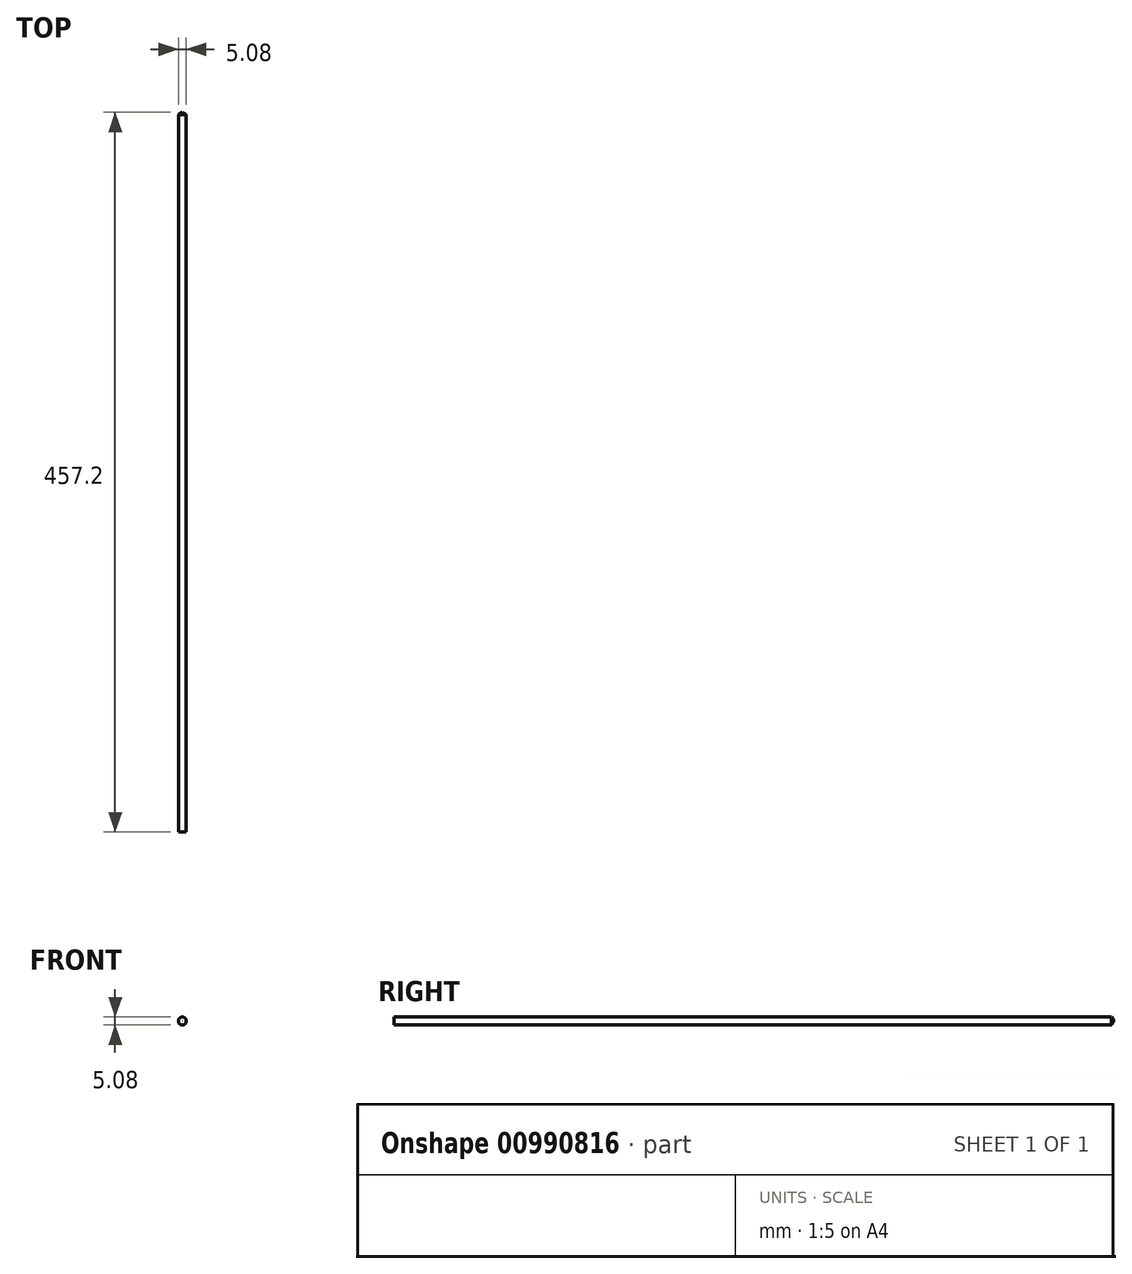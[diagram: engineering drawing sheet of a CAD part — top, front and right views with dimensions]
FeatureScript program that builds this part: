
annotation { "Feature Type Name" : "Feature", "Feature Type Description" : "" }
export const myFeature = defineFeature(function(context is Context, id is Id, definition is map)
    precondition{}
    {
        {
            var Q0;
            Q0=qCreatedBy(makeId("Front.planeOp"),FACE);
            var sketch = newSketch(context, id + "F0", { "sketchPlane" : qUnion([Q0])});
            skCircle(sketch, "E0", {"center": v(0, 0) * mm, "radius": 2.54 * mm});
            skSolve(sketch);
        }
        {
            var Q0;
            Q0 = qSketchRegion(id + "F0", true);
            extrude(context, id + "F1", {"entities" : qUnion([Q0]), "depth" : 457.2 * mm, "offsetDistance" : 25.4 * mm});
        }
        {
            var Q0;
            Q0=makeQuery(id+"F1.opExtrude","CAP_EDGE",EDGE,{"disambiguationData":[OSD([sQuery(id+"F0.wireOp",EDGE,"E0")])],"isStart":true});
            chamfer(context, id + "F2", {"entities" : qUnion([Q0]), "chamferType" : ChamferType.OFFSET_ANGLE, "width" : 1.52 * mm, "oppositeDirection" : false, "angle" : 59 * degree, "tangentPropagation" : true});
        }
    });
